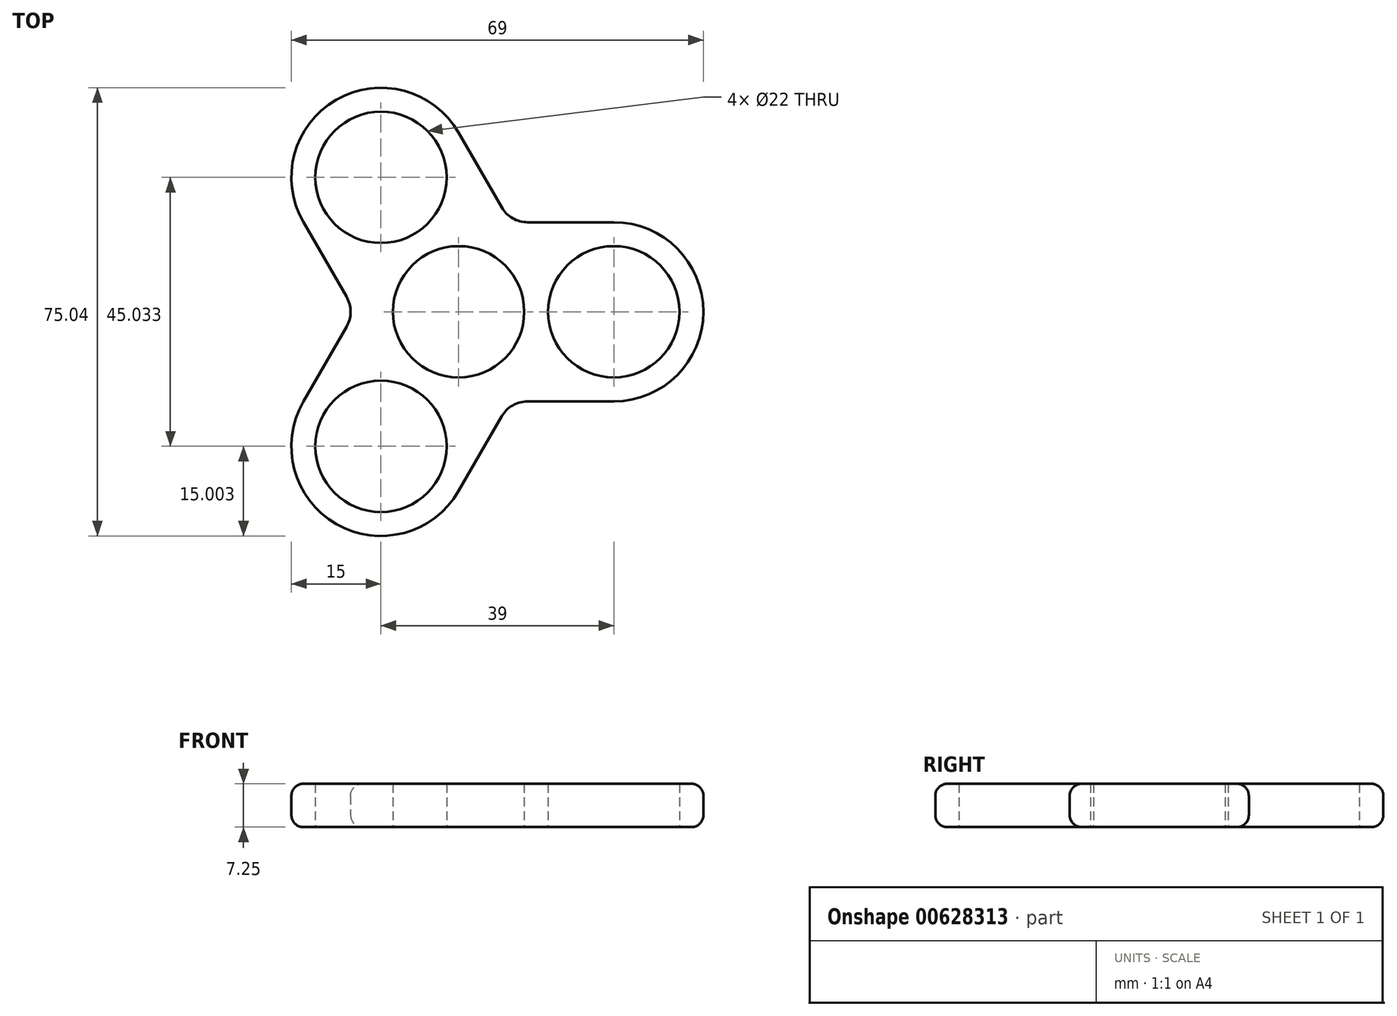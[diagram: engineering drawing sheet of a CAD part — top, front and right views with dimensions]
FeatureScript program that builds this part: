
annotation { "Feature Type Name" : "Feature", "Feature Type Description" : "" }
export const myFeature = defineFeature(function(context is Context, id is Id, definition is map)
    precondition{}
    {
        {
            var Q0;
            Q0=qCreatedBy(makeId("Top.planeOp"),FACE);
            var sketch = newSketch(context, id + "F0", { "sketchPlane" : qUnion([Q0])});
            skCircle(sketch, "E0", {"center": v(0, 0) * mm, "radius": 11 * mm});
            skCircle(sketch, "E1", {"center": v(26, 0) * mm, "radius": 11 * mm});
            skLineSegment(sketch, "E2", {"start": v(0, 0) * mm, "end": v(26, 0) * mm});
            skArc(sketch, "E3.0", {"start": v(13, 7.48) * mm, "mid": v(13, 7.5) * mm, "end": v(13, 7.5) * mm});
            skArc(sketch, "E4.0", {"start": v(26, -15) * mm, "mid": v(41, 0) * mm, "end": v(26, 15) * mm});
            skLineSegment(sketch, "E5", {"start": v(8.66, 15) * mm, "end": v(26, 15) * mm});
            skLineSegment(sketch, "E6", {"start": v(8.66, -15) * mm, "end": v(26, -15) * mm});
            skLineSegment(sketch, "E7.1.0", {"start": v(-17.32, 0) * mm, "end": v(-26, 15.02) * mm});
            skArc(sketch, "E7.1.1", {"start": v(0, 30.02) * mm, "mid": v(-20.5, 35.5) * mm, "end": v(-26, 15.02) * mm});
            skLineSegment(sketch, "E7.1.2", {"start": v(8.66, 15) * mm, "end": v(0, 30.02) * mm});
            skCircle(sketch, "E7.1.3", {"center": v(-13, 22.52) * mm, "radius": 11 * mm});
            skLineSegment(sketch, "E7.2.0", {"start": v(8.66, -15) * mm, "end": v(0, -30.02) * mm});
            skArc(sketch, "E7.2.1", {"start": v(-26, -15.02) * mm, "mid": v(-20.5, -35.5) * mm, "end": v(0, -30.02) * mm});
            skLineSegment(sketch, "E7.2.2", {"start": v(-17.32, 0) * mm, "end": v(-26, -15.02) * mm});
            skCircle(sketch, "E7.2.3", {"center": v(-13, -22.52) * mm, "radius": 11 * mm});
            skPoint(sketch, "E8.orphan", {"position": v(-13, -7.5) * mm});
            skPoint(sketch, "E9.orphan", {"position": v(-13, 7.5) * mm});
            skPoint(sketch, "E10.orphan", {"position": v(0, 15) * mm});
            skPoint(sketch, "E11.orphan", {"position": v(13, 7.5) * mm});
            skPoint(sketch, "E12.orphan", {"position": v(13, -7.5) * mm});
            skPoint(sketch, "E13.orphan", {"position": v(0, -15) * mm});
            skPoint(sketch, "E14.orphan", {"position": v(-12.98, 7.52) * mm});
            skPoint(sketch, "E15.orphan", {"position": v(-0.02, 15) * mm});
            skPoint(sketch, "E16.orphan", {"position": v(-0.02, -15) * mm});
            skPoint(sketch, "E17.orphan", {"position": v(-12.98, -7.52) * mm});
            skArc(sketch, "E18.trimOffspring", {"start": v(0, 15) * mm, "mid": v(0, 15) * mm, "end": v(-0.02, 15) * mm});
            skArc(sketch, "E19.trimOffspring", {"start": v(-12.98, 7.52) * mm, "mid": v(-12.99, 7.5) * mm, "end": v(-13, 7.5) * mm});
            skArc(sketch, "E20.trimOffspring", {"start": v(-13, -7.5) * mm, "mid": v(-12.99, -7.5) * mm, "end": v(-12.98, -7.52) * mm});
            skArc(sketch, "E21.trimOffspring", {"start": v(-0.02, -15) * mm, "mid": v(0, -15) * mm, "end": v(0, -15) * mm});
            skArc(sketch, "E22.trimOffspring", {"start": v(13, -7.5) * mm, "mid": v(13, -7.5) * mm, "end": v(13, -7.48) * mm});
            skSolve(sketch);
        }
        {
            var Q0;
            Q0=makeQuery(id+"F0.imprint","IMPRINT",FACE,{"disambiguationData":[TD([[makeQuery(id+"F0.imprint","IMPRINT",EDGE,{"derivedFrom":sQuery(id+"F0.wireOp",EDGE,"E0")}),-1.0]])]});
            extrude(context, id + "F1", {"entities" : qUnion([Q0]), "depth" : 7.25 * mm, "offsetDistance" : 25 * mm});
        }
        {
            var Q0;
            Q0=makeQuery(id+"F1.opExtrude","SWEPT_EDGE",EDGE,{"disambiguationData":[OSD([sQuery(id+"F0.wireOp",EDGE,"E5"),sQuery(id+"F0.wireOp",EDGE,"E7.1.2")])]});
            var Q1;
            Q1=makeQuery(id+"F1.opExtrude","SWEPT_EDGE",EDGE,{"disambiguationData":[OSD([sQuery(id+"F0.wireOp",EDGE,"E7.1.0"),sQuery(id+"F0.wireOp",EDGE,"E7.2.2")])]});
            var Q2;
            Q2=makeQuery(id+"F1.opExtrude","SWEPT_EDGE",EDGE,{"disambiguationData":[OSD([sQuery(id+"F0.wireOp",EDGE,"E6"),sQuery(id+"F0.wireOp",EDGE,"E7.2.0")])]});
            fillet(context, id + "F2", {"entities" : qUnion([Q0, Q1, Q2]), "radius" : 5 * mm, "tangentPropagation" : true, "allowEdgeOverflow" : false});
        }
        {
            var Q0;
            Q0=makeQuery(id+"F1.opExtrude","CAP_EDGE",EDGE,{"disambiguationData":[OSD([sQuery(id+"F0.wireOp",EDGE,"E7.2.0")])],"isStart":false});
            var Q1;
            Q1=makeQuery(id+"F1.opExtrude","CAP_EDGE",EDGE,{"disambiguationData":[OSD([sQuery(id+"F0.wireOp",EDGE,"E7.2.1")])],"isStart":false});
            var Q2;
            Q2=makeQuery(id+"F1.opExtrude","CAP_EDGE",EDGE,{"disambiguationData":[OSD([sQuery(id+"F0.wireOp",EDGE,"E7.2.2")])],"isStart":false});
            var Q3;
            {var subQ0=sQuery(id+"F0.wireOp",EDGE,"E7.2.2");var subQ1=sQuery(id+"F0.wireOp",EDGE,"E7.1.0");Q3=makeQuery(id+"F2.opFillet","BLEND_EDGE",EDGE,{"blendedFrom":[makeQuery(id+"F1.opExtrude","SWEPT_EDGE",EDGE,{"disambiguationData":[OSD([subQ1,subQ0])]}),makeQuery(id+"F1.opExtrude","CAP_FACE",FACE,{"disambiguationData":[OSD([sQuery(id+"F0.wireOp",EDGE,"E0"),sQuery(id+"F0.wireOp",EDGE,"E1"),sQuery(id+"F0.wireOp",EDGE,"E4.0"),sQuery(id+"F0.wireOp",EDGE,"E5"),sQuery(id+"F0.wireOp",EDGE,"E6"),subQ1,sQuery(id+"F0.wireOp",EDGE,"E7.1.1"),sQuery(id+"F0.wireOp",EDGE,"E7.1.2"),sQuery(id+"F0.wireOp",EDGE,"E7.1.3"),sQuery(id+"F0.wireOp",EDGE,"E7.2.0"),sQuery(id+"F0.wireOp",EDGE,"E7.2.1"),subQ0,sQuery(id+"F0.wireOp",EDGE,"E7.2.3")])],"isStart":false})],"blendedInto":[makeQuery(id+"F1.opExtrude","CAP_FACE",FACE,{"disambiguationData":[OSD([sQuery(id+"F0.wireOp",EDGE,"E0"),sQuery(id+"F0.wireOp",EDGE,"E1"),sQuery(id+"F0.wireOp",EDGE,"E4.0"),sQuery(id+"F0.wireOp",EDGE,"E5"),sQuery(id+"F0.wireOp",EDGE,"E6"),subQ1,sQuery(id+"F0.wireOp",EDGE,"E7.1.1"),sQuery(id+"F0.wireOp",EDGE,"E7.1.2"),sQuery(id+"F0.wireOp",EDGE,"E7.1.3"),sQuery(id+"F0.wireOp",EDGE,"E7.2.0"),sQuery(id+"F0.wireOp",EDGE,"E7.2.1"),subQ0,sQuery(id+"F0.wireOp",EDGE,"E7.2.3")])],"isStart":false})]});}
            var Q4;
            Q4=makeQuery(id+"F1.opExtrude","CAP_EDGE",EDGE,{"disambiguationData":[OSD([sQuery(id+"F0.wireOp",EDGE,"E7.1.0")])],"isStart":false});
            var Q5;
            Q5=makeQuery(id+"F1.opExtrude","CAP_EDGE",EDGE,{"disambiguationData":[OSD([sQuery(id+"F0.wireOp",EDGE,"E7.1.1")])],"isStart":false});
            var Q6;
            Q6=makeQuery(id+"F1.opExtrude","CAP_EDGE",EDGE,{"disambiguationData":[OSD([sQuery(id+"F0.wireOp",EDGE,"E7.1.2")])],"isStart":false});
            var Q7;
            Q7=makeQuery(id+"F1.opExtrude","CAP_EDGE",EDGE,{"disambiguationData":[OSD([sQuery(id+"F0.wireOp",EDGE,"E5")])],"isStart":false});
            var Q8;
            Q8=makeQuery(id+"F1.opExtrude","CAP_EDGE",EDGE,{"disambiguationData":[OSD([sQuery(id+"F0.wireOp",EDGE,"E4.0")])],"isStart":false});
            var Q9;
            Q9=makeQuery(id+"F1.opExtrude","CAP_EDGE",EDGE,{"disambiguationData":[OSD([sQuery(id+"F0.wireOp",EDGE,"E6")])],"isStart":false});
            var Q10;
            {var subQ0=sQuery(id+"F0.wireOp",EDGE,"E7.2.0");var subQ1=sQuery(id+"F0.wireOp",EDGE,"E6");Q10=makeQuery(id+"F2.opFillet","BLEND_EDGE",EDGE,{"blendedFrom":[makeQuery(id+"F1.opExtrude","SWEPT_EDGE",EDGE,{"disambiguationData":[OSD([subQ1,subQ0])]}),makeQuery(id+"F1.opExtrude","CAP_FACE",FACE,{"disambiguationData":[OSD([sQuery(id+"F0.wireOp",EDGE,"E0"),sQuery(id+"F0.wireOp",EDGE,"E1"),sQuery(id+"F0.wireOp",EDGE,"E4.0"),sQuery(id+"F0.wireOp",EDGE,"E5"),subQ1,sQuery(id+"F0.wireOp",EDGE,"E7.1.0"),sQuery(id+"F0.wireOp",EDGE,"E7.1.1"),sQuery(id+"F0.wireOp",EDGE,"E7.1.2"),sQuery(id+"F0.wireOp",EDGE,"E7.1.3"),subQ0,sQuery(id+"F0.wireOp",EDGE,"E7.2.1"),sQuery(id+"F0.wireOp",EDGE,"E7.2.2"),sQuery(id+"F0.wireOp",EDGE,"E7.2.3")])],"isStart":false})],"blendedInto":[makeQuery(id+"F1.opExtrude","CAP_FACE",FACE,{"disambiguationData":[OSD([sQuery(id+"F0.wireOp",EDGE,"E0"),sQuery(id+"F0.wireOp",EDGE,"E1"),sQuery(id+"F0.wireOp",EDGE,"E4.0"),sQuery(id+"F0.wireOp",EDGE,"E5"),subQ1,sQuery(id+"F0.wireOp",EDGE,"E7.1.0"),sQuery(id+"F0.wireOp",EDGE,"E7.1.1"),sQuery(id+"F0.wireOp",EDGE,"E7.1.2"),sQuery(id+"F0.wireOp",EDGE,"E7.1.3"),subQ0,sQuery(id+"F0.wireOp",EDGE,"E7.2.1"),sQuery(id+"F0.wireOp",EDGE,"E7.2.2"),sQuery(id+"F0.wireOp",EDGE,"E7.2.3")])],"isStart":false})]});}
            var Q11;
            {var subQ0=sQuery(id+"F0.wireOp",EDGE,"E7.1.2");var subQ1=sQuery(id+"F0.wireOp",EDGE,"E5");Q11=makeQuery(id+"F2.opFillet","BLEND_EDGE",EDGE,{"blendedFrom":[makeQuery(id+"F1.opExtrude","SWEPT_EDGE",EDGE,{"disambiguationData":[OSD([subQ1,subQ0])]}),makeQuery(id+"F1.opExtrude","CAP_FACE",FACE,{"disambiguationData":[OSD([sQuery(id+"F0.wireOp",EDGE,"E0"),sQuery(id+"F0.wireOp",EDGE,"E1"),sQuery(id+"F0.wireOp",EDGE,"E4.0"),subQ1,sQuery(id+"F0.wireOp",EDGE,"E6"),sQuery(id+"F0.wireOp",EDGE,"E7.1.0"),sQuery(id+"F0.wireOp",EDGE,"E7.1.1"),subQ0,sQuery(id+"F0.wireOp",EDGE,"E7.1.3"),sQuery(id+"F0.wireOp",EDGE,"E7.2.0"),sQuery(id+"F0.wireOp",EDGE,"E7.2.1"),sQuery(id+"F0.wireOp",EDGE,"E7.2.2"),sQuery(id+"F0.wireOp",EDGE,"E7.2.3")])],"isStart":false})],"blendedInto":[makeQuery(id+"F1.opExtrude","CAP_FACE",FACE,{"disambiguationData":[OSD([sQuery(id+"F0.wireOp",EDGE,"E0"),sQuery(id+"F0.wireOp",EDGE,"E1"),sQuery(id+"F0.wireOp",EDGE,"E4.0"),subQ1,sQuery(id+"F0.wireOp",EDGE,"E6"),sQuery(id+"F0.wireOp",EDGE,"E7.1.0"),sQuery(id+"F0.wireOp",EDGE,"E7.1.1"),subQ0,sQuery(id+"F0.wireOp",EDGE,"E7.1.3"),sQuery(id+"F0.wireOp",EDGE,"E7.2.0"),sQuery(id+"F0.wireOp",EDGE,"E7.2.1"),sQuery(id+"F0.wireOp",EDGE,"E7.2.2"),sQuery(id+"F0.wireOp",EDGE,"E7.2.3")])],"isStart":false})]});}
            var Q12;
            Q12=makeQuery(id+"F1.opExtrude","CAP_EDGE",EDGE,{"disambiguationData":[OSD([sQuery(id+"F0.wireOp",EDGE,"E6")])],"isStart":true});
            var Q13;
            Q13=makeQuery(id+"F1.opExtrude","CAP_EDGE",EDGE,{"disambiguationData":[OSD([sQuery(id+"F0.wireOp",EDGE,"E7.2.0")])],"isStart":true});
            var Q14;
            Q14=makeQuery(id+"F1.opExtrude","CAP_EDGE",EDGE,{"disambiguationData":[OSD([sQuery(id+"F0.wireOp",EDGE,"E7.2.2")])],"isStart":true});
            var Q15;
            Q15=makeQuery(id+"F1.opExtrude","CAP_EDGE",EDGE,{"disambiguationData":[OSD([sQuery(id+"F0.wireOp",EDGE,"E7.2.1")])],"isStart":true});
            var Q16;
            Q16=makeQuery(id+"F1.opExtrude","CAP_EDGE",EDGE,{"disambiguationData":[OSD([sQuery(id+"F0.wireOp",EDGE,"E4.0")])],"isStart":true});
            var Q17;
            Q17=makeQuery(id+"F1.opExtrude","CAP_EDGE",EDGE,{"disambiguationData":[OSD([sQuery(id+"F0.wireOp",EDGE,"E5")])],"isStart":true});
            var Q18;
            Q18=makeQuery(id+"F1.opExtrude","CAP_EDGE",EDGE,{"disambiguationData":[OSD([sQuery(id+"F0.wireOp",EDGE,"E7.1.1")])],"isStart":true});
            var Q19;
            Q19=makeQuery(id+"F1.opExtrude","CAP_EDGE",EDGE,{"disambiguationData":[OSD([sQuery(id+"F0.wireOp",EDGE,"E7.1.2")])],"isStart":true});
            var Q20;
            Q20=makeQuery(id+"F1.opExtrude","CAP_EDGE",EDGE,{"disambiguationData":[OSD([sQuery(id+"F0.wireOp",EDGE,"E7.1.0")])],"isStart":true});
            var Q21;
            {var subQ0=sQuery(id+"F0.wireOp",EDGE,"E7.2.2");var subQ1=sQuery(id+"F0.wireOp",EDGE,"E7.1.0");Q21=makeQuery(id+"F2.opFillet","BLEND_EDGE",EDGE,{"blendedFrom":[makeQuery(id+"F1.opExtrude","SWEPT_EDGE",EDGE,{"disambiguationData":[OSD([subQ1,subQ0])]}),makeQuery(id+"F1.opExtrude","CAP_FACE",FACE,{"disambiguationData":[OSD([sQuery(id+"F0.wireOp",EDGE,"E0"),sQuery(id+"F0.wireOp",EDGE,"E1"),sQuery(id+"F0.wireOp",EDGE,"E4.0"),sQuery(id+"F0.wireOp",EDGE,"E5"),sQuery(id+"F0.wireOp",EDGE,"E6"),subQ1,sQuery(id+"F0.wireOp",EDGE,"E7.1.1"),sQuery(id+"F0.wireOp",EDGE,"E7.1.2"),sQuery(id+"F0.wireOp",EDGE,"E7.1.3"),sQuery(id+"F0.wireOp",EDGE,"E7.2.0"),sQuery(id+"F0.wireOp",EDGE,"E7.2.1"),subQ0,sQuery(id+"F0.wireOp",EDGE,"E7.2.3")])],"isStart":true})],"blendedInto":[makeQuery(id+"F1.opExtrude","CAP_FACE",FACE,{"disambiguationData":[OSD([sQuery(id+"F0.wireOp",EDGE,"E0"),sQuery(id+"F0.wireOp",EDGE,"E1"),sQuery(id+"F0.wireOp",EDGE,"E4.0"),sQuery(id+"F0.wireOp",EDGE,"E5"),sQuery(id+"F0.wireOp",EDGE,"E6"),subQ1,sQuery(id+"F0.wireOp",EDGE,"E7.1.1"),sQuery(id+"F0.wireOp",EDGE,"E7.1.2"),sQuery(id+"F0.wireOp",EDGE,"E7.1.3"),sQuery(id+"F0.wireOp",EDGE,"E7.2.0"),sQuery(id+"F0.wireOp",EDGE,"E7.2.1"),subQ0,sQuery(id+"F0.wireOp",EDGE,"E7.2.3")])],"isStart":true})]});}
            var Q22;
            {var subQ0=sQuery(id+"F0.wireOp",EDGE,"E7.1.2");var subQ1=sQuery(id+"F0.wireOp",EDGE,"E5");Q22=makeQuery(id+"F2.opFillet","BLEND_EDGE",EDGE,{"blendedFrom":[makeQuery(id+"F1.opExtrude","SWEPT_EDGE",EDGE,{"disambiguationData":[OSD([subQ1,subQ0])]}),makeQuery(id+"F1.opExtrude","CAP_FACE",FACE,{"disambiguationData":[OSD([sQuery(id+"F0.wireOp",EDGE,"E0"),sQuery(id+"F0.wireOp",EDGE,"E1"),sQuery(id+"F0.wireOp",EDGE,"E4.0"),subQ1,sQuery(id+"F0.wireOp",EDGE,"E6"),sQuery(id+"F0.wireOp",EDGE,"E7.1.0"),sQuery(id+"F0.wireOp",EDGE,"E7.1.1"),subQ0,sQuery(id+"F0.wireOp",EDGE,"E7.1.3"),sQuery(id+"F0.wireOp",EDGE,"E7.2.0"),sQuery(id+"F0.wireOp",EDGE,"E7.2.1"),sQuery(id+"F0.wireOp",EDGE,"E7.2.2"),sQuery(id+"F0.wireOp",EDGE,"E7.2.3")])],"isStart":true})],"blendedInto":[makeQuery(id+"F1.opExtrude","CAP_FACE",FACE,{"disambiguationData":[OSD([sQuery(id+"F0.wireOp",EDGE,"E0"),sQuery(id+"F0.wireOp",EDGE,"E1"),sQuery(id+"F0.wireOp",EDGE,"E4.0"),subQ1,sQuery(id+"F0.wireOp",EDGE,"E6"),sQuery(id+"F0.wireOp",EDGE,"E7.1.0"),sQuery(id+"F0.wireOp",EDGE,"E7.1.1"),subQ0,sQuery(id+"F0.wireOp",EDGE,"E7.1.3"),sQuery(id+"F0.wireOp",EDGE,"E7.2.0"),sQuery(id+"F0.wireOp",EDGE,"E7.2.1"),sQuery(id+"F0.wireOp",EDGE,"E7.2.2"),sQuery(id+"F0.wireOp",EDGE,"E7.2.3")])],"isStart":true})]});}
            var Q23;
            {var subQ0=sQuery(id+"F0.wireOp",EDGE,"E7.2.0");var subQ1=sQuery(id+"F0.wireOp",EDGE,"E6");Q23=makeQuery(id+"F2.opFillet","BLEND_EDGE",EDGE,{"blendedFrom":[makeQuery(id+"F1.opExtrude","SWEPT_EDGE",EDGE,{"disambiguationData":[OSD([subQ1,subQ0])]}),makeQuery(id+"F1.opExtrude","CAP_FACE",FACE,{"disambiguationData":[OSD([sQuery(id+"F0.wireOp",EDGE,"E0"),sQuery(id+"F0.wireOp",EDGE,"E1"),sQuery(id+"F0.wireOp",EDGE,"E4.0"),sQuery(id+"F0.wireOp",EDGE,"E5"),subQ1,sQuery(id+"F0.wireOp",EDGE,"E7.1.0"),sQuery(id+"F0.wireOp",EDGE,"E7.1.1"),sQuery(id+"F0.wireOp",EDGE,"E7.1.2"),sQuery(id+"F0.wireOp",EDGE,"E7.1.3"),subQ0,sQuery(id+"F0.wireOp",EDGE,"E7.2.1"),sQuery(id+"F0.wireOp",EDGE,"E7.2.2"),sQuery(id+"F0.wireOp",EDGE,"E7.2.3")])],"isStart":true})],"blendedInto":[makeQuery(id+"F1.opExtrude","CAP_FACE",FACE,{"disambiguationData":[OSD([sQuery(id+"F0.wireOp",EDGE,"E0"),sQuery(id+"F0.wireOp",EDGE,"E1"),sQuery(id+"F0.wireOp",EDGE,"E4.0"),sQuery(id+"F0.wireOp",EDGE,"E5"),subQ1,sQuery(id+"F0.wireOp",EDGE,"E7.1.0"),sQuery(id+"F0.wireOp",EDGE,"E7.1.1"),sQuery(id+"F0.wireOp",EDGE,"E7.1.2"),sQuery(id+"F0.wireOp",EDGE,"E7.1.3"),subQ0,sQuery(id+"F0.wireOp",EDGE,"E7.2.1"),sQuery(id+"F0.wireOp",EDGE,"E7.2.2"),sQuery(id+"F0.wireOp",EDGE,"E7.2.3")])],"isStart":true})]});}
            fillet(context, id + "F3", {"entities" : qUnion([Q0, Q1, Q2, Q3, Q4, Q5, Q6, Q7, Q8, Q9, Q10, Q11, Q12, Q13, Q14, Q15, Q16, Q17, Q18, Q19, Q20, Q21, Q22, Q23]), "radius" : 2 * mm, "tangentPropagation" : true, "allowEdgeOverflow" : false});
        }
    });
